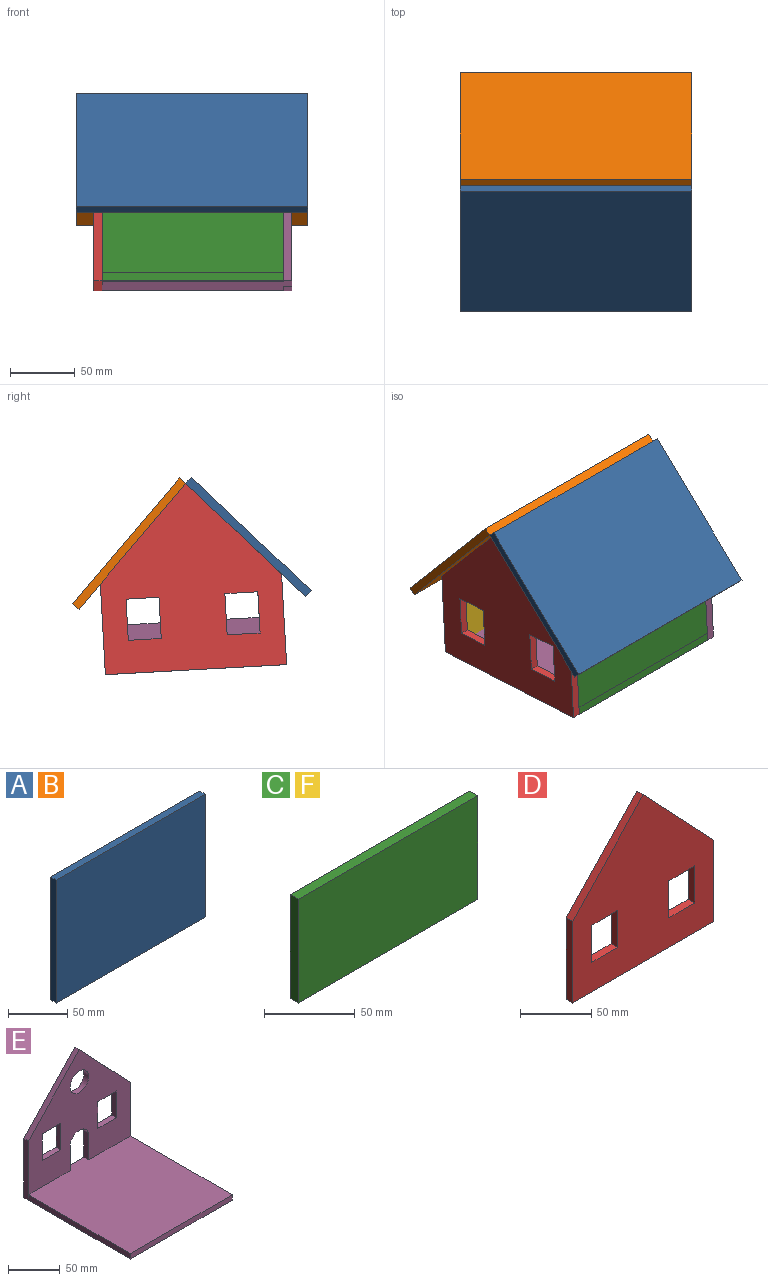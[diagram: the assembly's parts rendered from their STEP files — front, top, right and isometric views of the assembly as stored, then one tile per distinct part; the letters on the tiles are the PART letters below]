
ASSEMBLY  parts=6 mates=5
PART A: 6 faces, bbox 177.8x6.4x127 mm
  f0: plane 127x6.35mm, normal (1,0,0), area 806.5mm2, adj f1,f3,f4,f5
  f1: plane 177.8x6.35mm, normal (0,0,1), area 1129mm2, adj f0,f2,f4,f5
  f2: plane 127x6.35mm, normal (-1,0,0), area 806.5mm2, adj f1,f3,f4,f5
  f3: plane 177.8x6.35mm, normal (0,0,-1), area 1129mm2, adj f0,f2,f4,f5
  f4: plane 177.8x127mm, normal (0,-1,0), area 22580.6mm2, adj f0,f1,f2,f3
  f5: plane 177.8x127mm, normal (0,1,0), area 22580.6mm2, adj f0,f1,f2,f3
PART B: same geometry as A
PART C: 6 faces, bbox 139.7x6.4x69.9 mm
  f0: plane 69.85x6.35mm, normal (1,0,0), area 443.5mm2, adj f1,f3,f4,f5
  f1: plane 139.7x6.35mm, normal (0,0,1), area 887.1mm2, adj f0,f2,f4,f5
  f2: plane 69.85x6.35mm, normal (-1,0,0), area 443.5mm2, adj f1,f3,f4,f5
  f3: plane 139.7x6.35mm, normal (0,0,-1), area 887.1mm2, adj f0,f2,f4,f5
  f4: plane 139.7x69.85mm, normal (0,-1,0), area 9758mm2, adj f0,f1,f2,f3
  f5: plane 139.7x69.85mm, normal (0,1,0), area 9758mm2, adj f0,f1,f2,f3
PART D: 15 faces, bbox 139.7x6.4x143.6 mm
  f0: plane 25.4x6.35mm, normal (0,0,-1), area 161.3mm2, adj f1,f12,f13,f14
  f1: plane 31.75x6.35mm, normal (-1,0,0), area 201.6mm2, adj f0,f2,f13,f14
  f2: plane 25.4x6.35mm, normal (0,0,1), area 161.3mm2, adj f1,f12,f13,f14
  f3: plane 25.4x6.35mm, normal (0,0,-1), area 161.3mm2, adj f4,f10,f13,f14
  f4: plane 31.75x6.35mm, normal (-1,0,0), area 201.6mm2, adj f3,f5,f13,f14
  f5: plane 25.4x6.35mm, normal (0,0,1), area 161.3mm2, adj f4,f10,f13,f14
  f6: plane 139.7x6.35mm, normal (0,0,-1), area 887.1mm2, adj f7,f11,f13,f14
  f7: plane 69.85x6.35mm, normal (1,0,0), area 443.5mm2, adj f6,f8,f13,f14
  f8: plane 73.78x69.85mm, normal (0.73,0,0.69), area 645.2mm2, adj f7,f9,f13,f14
  f9: plane 73.78x69.85mm, normal (-0.73,0,0.69), area 645.2mm2, adj f8,f11,f13,f14
  f10: plane 31.75x6.35mm, normal (1,0,0), area 201.6mm2, adj f3,f5,f13,f14
  f11: plane 69.85x6.35mm, normal (-1,0,0), area 443.5mm2, adj f6,f9,f13,f14
  f12: plane 31.75x6.35mm, normal (1,0,0), area 201.6mm2, adj f0,f2,f13,f14
  f13: plane 143.63x139.7mm, normal (0,-1,0), area 13298.7mm2, adj f0,f1,f2,f3,f4,f5,f6,f7
  f14: plane 143.63x139.7mm, normal (0,1,0), area 13298.7mm2, adj f0,f1,f2,f3,f4,f5,f6,f7
PART E: 29 faces, bbox 139.7x146.1x143.6 mm
  f0: plane 57.15x0.08mm, normal (0,-1,0), area 4.4mm2, adj f2,f11,f12,f26
  f1: plane 57.15x0.07mm, normal (0,-1,0), area 4.2mm2, adj f3,f4,f17,f26
  f2: plane 6.35x0.08mm, normal (-1,0,0), area 0.5mm2, adj f0,f11,f20,f26
  f3: plane 6.35x0.07mm, normal (1,0,0), area 0.5mm2, adj f1,f4,f20,f26
  f4: plane 57.15x6.35mm, normal (0,0,-1), area 362.9mm2, adj f1,f3,f17,f20
  f5: plane 31.75x6.35mm, normal (-1,0,0), area 201.6mm2, adj f6,f15,f19,f20
  f6: plane 25.4x6.35mm, normal (0,0,1), area 161.3mm2, adj f5,f7,f19,f20
  f7: plane 31.75x6.35mm, normal (1,0,0), area 201.6mm2, adj f6,f15,f19,f20
  f8: plane 31.75x6.35mm, normal (-1,0,0), area 201.6mm2, adj f9,f16,f19,f20
  f9: plane 25.4x6.35mm, normal (0,0,1), area 161.3mm2, adj f8,f10,f19,f20
  f10: plane 31.75x6.35mm, normal (1,0,0), area 201.6mm2, adj f9,f16,f19,f20
  f11: plane 57.15x6.35mm, normal (0,0,-1), area 362.9mm2, adj f0,f2,f12,f20
  f12: plane 69.85x6.35mm, normal (1,0,0), area 443.5mm2, adj f0,f11,f13,f19,f20,f27
  f13: plane 73.78x69.85mm, normal (0.73,0,0.69), area 645.2mm2, adj f12,f14,f19,f20
  f14: plane 73.77x69.85mm, normal (-0.73,0,0.69), area 645.1mm2, adj f13,f17,f19,f20
  f15: plane 25.4x6.35mm, normal (0,0,-1), area 161.3mm2, adj f5,f7,f19,f20
  f16: plane 25.4x6.35mm, normal (0,0,-1), area 161.3mm2, adj f8,f10,f19,f20
  f17: plane 69.85x6.35mm, normal (-1,0,0), area 443.5mm2, adj f1,f4,f14,f19,f20,f25
  f18: cylinder r=12.7mm len=25.4mm, axis (0,1,0), area 506.7mm2, adj f19,f20
  f19: plane 139.7x137.2mm, normal (0,-1,0), area 10902.7mm2, adj f5,f6,f7,f8,f9,f10,f12,f13
  f20: plane 143.63x139.7mm, normal (0,1,0), area 11798.4mm2, adj f2,f3,f4,f5,f6,f7,f8,f9
  f21: plane 31.67x6.35mm, normal (-1,0,0), area 201.1mm2, adj f19,f20,f22,f24
  f22: cylinder r=13.09mm len=25.4mm, axis (0,-1,0), area 220.4mm2, adj f19,f20,f21,f23
  f23: plane 31.68x6.35mm, normal (1,0,0), area 201.1mm2, adj f19,f20,f22,f24
  f24: plane 146.05x139.7mm, normal (0,0,1), area 19677.4mm2, adj f19,f20,f21,f23,f25,f27,f28
  f25: plane 139.7x6.35mm, normal (-1,0,0), area 887.1mm2, adj f17,f24,f26,f28
  f26: plane 146.05x139.7mm, normal (0,0,-1), area 19677.4mm2, adj f0,f1,f2,f3,f20,f25,f27,f28
  f27: plane 139.7x6.35mm, normal (1,0,0), area 887.1mm2, adj f12,f24,f26,f28
  f28: plane 139.7x6.35mm, normal (0,-1,0), area 887.1mm2, adj f24,f25,f26,f27
PART F: same geometry as C
PLACE A rot(axis=(-1,0,0),46.6deg) t=(-37.83,-192.33,202.42)mm
PLACE B rot(axis=(1,0,0),40.3deg) t=(-37.83,-100.31,201.7)mm
PLACE C rot(axis=(-1,0,0),3.2deg) t=(-37.2,-215.6,141.06)mm
PLACE D rot(axis=(-0.03,0.03,1),90deg) t=(-113.4,-152.2,137.55)mm
PLACE E rot(axis=(-0.03,-0.03,-1),90deg) t=(39,-152.2,137.51)mm
PLACE F rot(axis=(-1,0,0),3.2deg) t=(-37.2,-82.46,133.69)mm
MATE fastened B.f4 <-> E.f14  axis (0,-0.76,-0.65) through (51.07,-105.15,197.6)mm
MATE fastened F.f0 <-> E.f19  axis (1,0,0) through (32.65,-85.63,133.86)mm
MATE fastened C.f0 <-> E.f19  axis (1,0,0) through (32.65,-218.77,141.24)mm
MATE fastened D.f13 <-> C.f2  axis (1,0,0) through (-107.05,-221.94,141.41)mm
MATE fastened A.f5 <-> E.f13  axis (0,0.69,-0.73) through (51.07,-192.33,202.42)mm
